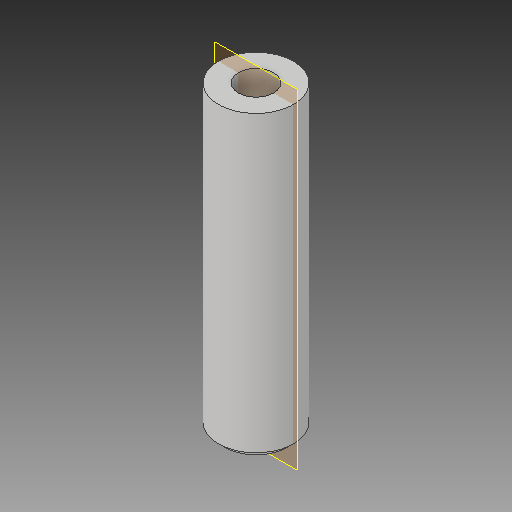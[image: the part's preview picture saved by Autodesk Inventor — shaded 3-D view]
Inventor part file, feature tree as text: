
AUTODESK INVENTOR PART (.ipt)
format: ipt  version: 2018 (Build 220112000, 112)  size: 82,432 bytes
history: native  units: mm
features: extrude x1, chamfer x1, sketch x1
ambient origin geometry x8: Origin, YZ Plane, XZ Plane, XY Plane, X Axis, Y Axis, Z Axis, Center Point
bodies: Solid1 (feature_tree)
feature tree (3):
  extrude  "Extrusion1"  Depth=2.0mm
  chamfer  "Chamfer1"  Distance=200.0mm
  sketch  "Sketch1"  dims[d0=50.0mm d1=23.5mm d2=200.0mm d3=0.0mm d4=4.0mm d5=2.0mm d6=45.0deg]
